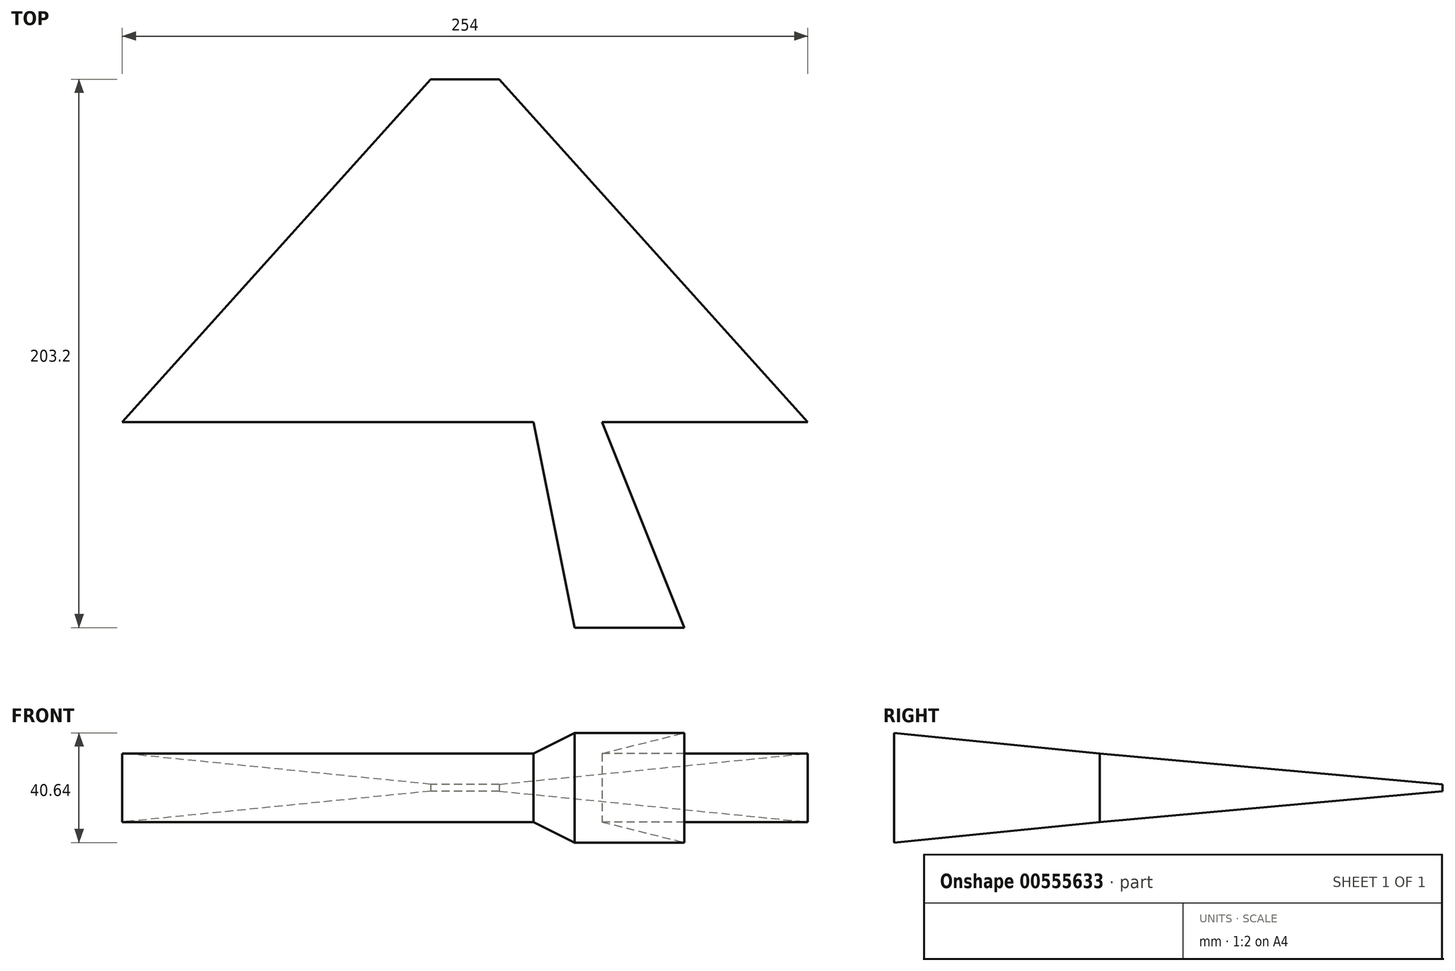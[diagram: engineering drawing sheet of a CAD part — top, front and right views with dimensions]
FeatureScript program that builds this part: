
annotation { "Feature Type Name" : "Feature", "Feature Type Description" : "" }
export const myFeature = defineFeature(function(context is Context, id is Id, definition is map)
    precondition{}
    {
        {
            var Q0;
            Q0=qCreatedBy(makeId("Front.planeOp"),FACE);
            var sketch = newSketch(context, id + "F0", { "sketchPlane" : qUnion([Q0])});
            skLineSegment(sketch, "E0.bottom", {"start": v(12.7, 1.27) * mm, "end": v(-12.7, 1.27) * mm});
            skLineSegment(sketch, "E0.top", {"start": v(12.7, -1.27) * mm, "end": v(-12.7, -1.27) * mm});
            skLineSegment(sketch, "E0.left", {"start": v(12.7, 1.27) * mm, "end": v(12.7, -1.27) * mm});
            skLineSegment(sketch, "E0.right", {"start": v(-12.7, 1.27) * mm, "end": v(-12.7, -1.27) * mm});
            skPoint(sketch, "E0.middle", {"position": v(0, 0) * mm});
            skSolve(sketch);
        }
        {
            var Q0;
            Q0=qCreatedBy(makeId("Front.planeOp"),FACE);
            cPlane(context, id + "F1", {"entities" : qUnion([Q0]), "cplaneType" : CPlaneType.OFFSET, "offset" : 127 * mm, "width" : 152.4 * mm, "height" : 152.4 * mm});
        }
        {
            var Q0;
            Q0=qCreatedBy(id+"F1.planeOp",FACE);
            var sketch = newSketch(context, id + "F2", { "sketchPlane" : qUnion([Q0])});
            skLineSegment(sketch, "E1.bottom", {"start": v(127, 12.7) * mm, "end": v(-127, 12.7) * mm});
            skLineSegment(sketch, "E1.top", {"start": v(127, -12.7) * mm, "end": v(-127, -12.7) * mm});
            skLineSegment(sketch, "E1.left", {"start": v(127, 12.7) * mm, "end": v(127, -12.7) * mm});
            skLineSegment(sketch, "E1.right", {"start": v(-127, 12.7) * mm, "end": v(-127, -12.7) * mm});
            skPoint(sketch, "E1.middle", {"position": v(0, 0) * mm});
            skSolve(sketch);
        }
        {
            var Q0;
            Q0=makeQuery(id+"F0.imprint","IMPRINT",FACE,{"disambiguationData":[TD([[makeQuery(id+"F0.imprint","IMPRINT",EDGE,{"derivedFrom":sQuery(id+"F0.wireOp",EDGE,"E0.bottom")}),1.0]])]});
            var Q1;
            Q1=makeQuery(id+"F2.imprint","IMPRINT",FACE,{"disambiguationData":[TD([[makeQuery(id+"F2.imprint","IMPRINT",EDGE,{"derivedFrom":sQuery(id+"F2.wireOp",EDGE,"E1.bottom")}),1.0]])]});
            loft(context, id + "F3", {"sheetProfilesArray" : [{ "sheetProfileEntities" : qUnion([Q0]) }, { "sheetProfileEntities" : qUnion([Q1]) }]});
        }
        {
            var Q0;
            Q0=makeQuery(id+"F3.opLoft","CAP_FACE",FACE,{"disambiguationData":[OSD([makeQuery(id+"F2.imprint","IMPRINT",FACE,{"disambiguationData":[TD([[makeQuery(id+"F2.imprint","IMPRINT",EDGE,{"derivedFrom":sQuery(id+"F2.wireOp",EDGE,"E1.bottom")}),1.0]])]})])],"isStart":true});
            var sketch = newSketch(context, id + "F4", { "sketchPlane" : qUnion([Q0])});
            skLineSegment(sketch, "E2.bottom", {"start": v(25.4, 12.7) * mm, "end": v(50.8, 12.7) * mm});
            skLineSegment(sketch, "E2.top", {"start": v(25.4, -12.7) * mm, "end": v(50.8, -12.7) * mm});
            skLineSegment(sketch, "E2.left", {"start": v(25.4, 12.7) * mm, "end": v(25.4, -12.7) * mm});
            skLineSegment(sketch, "E2.right", {"start": v(50.8, 12.7) * mm, "end": v(50.8, -12.7) * mm});
            skSolve(sketch);
        }
        {
            var Q0;
            Q0=qCreatedBy(id+"F1.planeOp",FACE);
            cPlane(context, id + "F5", {"entities" : qUnion([Q0]), "cplaneType" : CPlaneType.OFFSET, "offset" : 76.2 * mm, "width" : 152.4 * mm, "height" : 152.4 * mm});
        }
        {
            var Q0;
            Q0=qCreatedBy(id+"F5.planeOp",FACE);
            var sketch = newSketch(context, id + "F6", { "sketchPlane" : qUnion([Q0])});
            skLineSegment(sketch, "E3.bottom", {"start": v(40.64, 20.32) * mm, "end": v(81.28, 20.32) * mm});
            skLineSegment(sketch, "E3.top", {"start": v(40.64, -20.32) * mm, "end": v(81.28, -20.32) * mm});
            skLineSegment(sketch, "E3.left", {"start": v(40.64, 20.32) * mm, "end": v(40.64, -20.32) * mm});
            skLineSegment(sketch, "E3.right", {"start": v(81.28, 20.32) * mm, "end": v(81.28, -20.32) * mm});
            skLineSegment(sketch, "E4", {"start": v(0, 0) * mm, "end": v(40.64, 0) * mm, "construction": true});
            skSolve(sketch);
        }
        {
            var Q1;
            Q1=makeQuery(id+"F4.imprint","IMPRINT",FACE,{"disambiguationData":[TD([[makeQuery(id+"F4.imprint","IMPRINT",EDGE,{"derivedFrom":sQuery(id+"F4.wireOp",EDGE,"E2.bottom")}),1.0]])]});
            var Q2;
            Q2=makeQuery(id+"F6.imprint","IMPRINT",FACE,{"disambiguationData":[TD([[makeQuery(id+"F6.imprint","IMPRINT",EDGE,{"derivedFrom":sQuery(id+"F6.wireOp",EDGE,"E3.bottom")}),-1.0]])]});
            loft(context, id + "F7", {"operationType" : NewBodyOperationType.ADD, "sheetProfilesArray" : [{ "sheetProfileEntities" : qUnion([Q1]) }, { "sheetProfileEntities" : qUnion([Q2]) }]});
        }
    });
